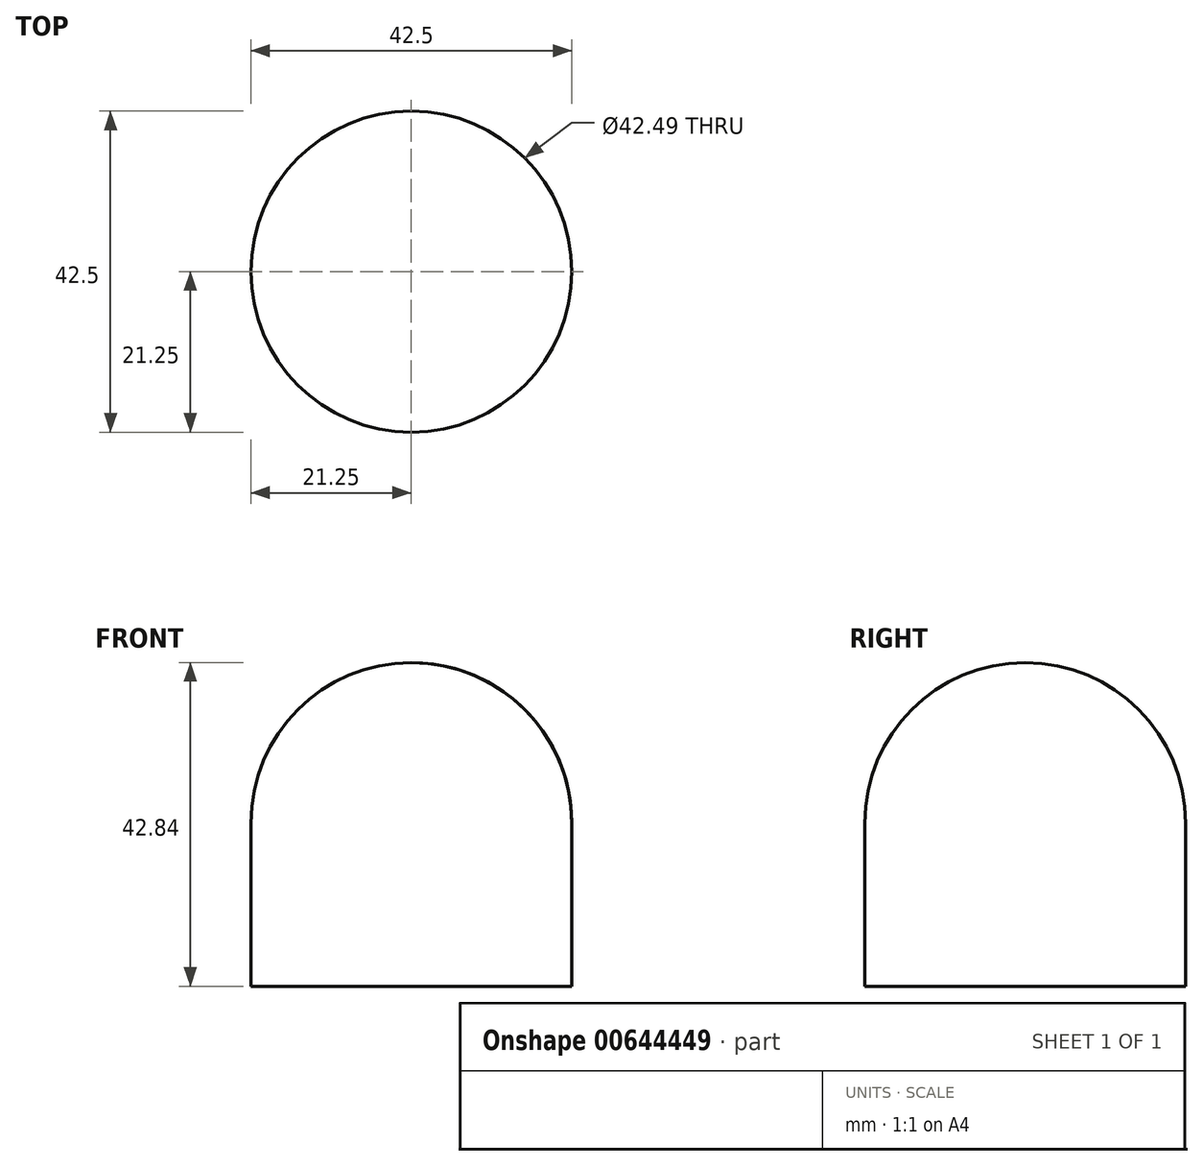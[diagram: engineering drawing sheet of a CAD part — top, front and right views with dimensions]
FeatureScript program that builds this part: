
annotation { "Feature Type Name" : "Feature", "Feature Type Description" : "" }
export const myFeature = defineFeature(function(context is Context, id is Id, definition is map)
    precondition{}
    {
        {
            var Q0;
            Q0=qCreatedBy(makeId("Front.planeOp"),FACE);
            var sketch = newSketch(context, id + "F0", { "sketchPlane" : qUnion([Q0])});
            skLineSegment(sketch, "E0", {"start": v(0, 159.75) * mm, "end": v(0, -127.56) * mm, "construction": true});
            skLineSegment(sketch, "E1", {"start": v(-21.25, 0) * mm, "end": v(-21.25, -21.59) * mm});
            skArc(sketch, "E2", {"start": v(0, 21.25) * mm, "mid": v(-15.02, 15.02) * mm, "end": v(-21.25, 0) * mm});
            skArc(sketch, "E3", {"start": v(-21.25, 0) * mm, "mid": v(15.02, -15.02) * mm, "end": v(0, 21.25) * mm, "construction": true});
            skSolve(sketch);
        }
        {
            var Q0;
            Q0 = qSketchRegion(id + "F0", true);
            var Q1;
            Q1=sQuery(id+"F0.wireOp",EDGE,"E1");
            var Q2;
            Q2=sQuery(id+"F0.wireOp",EDGE,"E2");
            var Q3;
            Q3=sQuery(id+"F0.wireOp",EDGE,"E0");
            revolve(context, id + "F1", {"bodyType" : ToolBodyType.SURFACE, "entities" : qUnion([Q0]), "surfaceEntities" : qUnion([Q1, Q2]), "axis" : qUnion([Q3]), "revolveType" : RevolveType.FULL});
        }
    });
